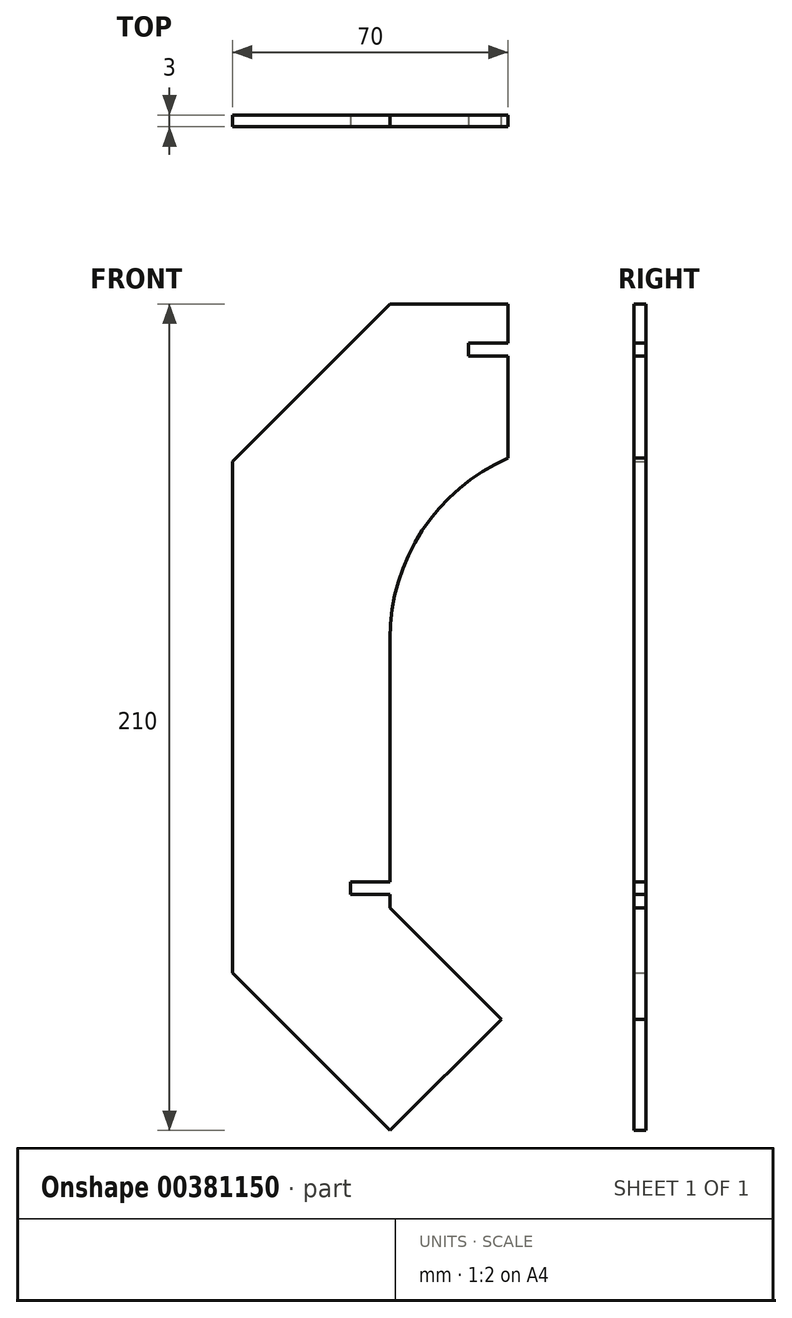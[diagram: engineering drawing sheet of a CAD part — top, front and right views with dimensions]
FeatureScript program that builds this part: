
annotation { "Feature Type Name" : "Feature", "Feature Type Description" : "" }
export const myFeature = defineFeature(function(context is Context, id is Id, definition is map)
    precondition{}
    {
        {
            var Q0;
            Q0=qCreatedBy(makeId("Front.planeOp"),FACE);
            var sketch = newSketch(context, id + "F0", { "sketchPlane" : qUnion([Q0])});
            skLineSegment(sketch, "E0", {"start": v(0, 0) * mm, "end": v(-50, 0) * mm});
            skLineSegment(sketch, "E1", {"start": v(-50, 0) * mm, "end": v(-90, -40) * mm});
            skLineSegment(sketch, "E2", {"start": v(-90, -40) * mm, "end": v(-90, -170) * mm});
            skLineSegment(sketch, "E3", {"start": v(-90, -170) * mm, "end": v(-50, -210) * mm});
            skLineSegment(sketch, "E4", {"start": v(-50, -210) * mm, "end": v(-21.72, -181.72) * mm});
            skLineSegment(sketch, "E5", {"start": v(-21.72, -181.72) * mm, "end": v(-50, -153.43) * mm});
            skArc(sketch, "E6", {"start": v(0, -35) * mm, "mid": v(-35.36, -49.64) * mm, "end": v(-50, -85) * mm});
            skLineSegment(sketch, "E7", {"start": v(-50, -85) * mm, "end": v(-50, -153.43) * mm});
            skLineSegment(sketch, "E8", {"start": v(0, 0) * mm, "end": v(0, -35) * mm});
            skSolve(sketch);
        }
        {
            var Q0;
            Q0=makeQuery(id+"F0.imprint","IMPRINT",FACE,{"disambiguationData":[TD([[makeQuery(id+"F0.imprint","IMPRINT",EDGE,{"derivedFrom":sQuery(id+"F0.wireOp",EDGE,"E0")}),1.0]])]});
            extrude(context, id + "F1", {"entities" : qUnion([Q0]), "endBound" : BoundingType.SYMMETRIC, "depth" : 3 * mm, "offsetDistance" : 25 * mm});
        }
        {
            var Q0;
            Q0=makeQuery(id+"F1.opExtrude","CAP_FACE",FACE,{"disambiguationData":[OSD([sQuery(id+"F0.wireOp",EDGE,"E0"),sQuery(id+"F0.wireOp",EDGE,"E1"),sQuery(id+"F0.wireOp",EDGE,"E2"),sQuery(id+"F0.wireOp",EDGE,"E3"),sQuery(id+"F0.wireOp",EDGE,"E4"),sQuery(id+"F0.wireOp",EDGE,"E5"),sQuery(id+"F0.wireOp",EDGE,"E6"),sQuery(id+"F0.wireOp",EDGE,"E7"),sQuery(id+"F0.wireOp",EDGE,"E8")])],"isStart":false});
            var sketch = newSketch(context, id + "F2", { "sketchPlane" : qUnion([Q0])});
            skLineSegment(sketch, "E9", {"start": v(-20, 0) * mm, "end": v(-20, -10) * mm});
            skLineSegment(sketch, "E10", {"start": v(-20, -10) * mm, "end": v(-30, -10) * mm});
            skLineSegment(sketch, "E11", {"start": v(-30, -10) * mm, "end": v(-30, -13.2) * mm});
            skLineSegment(sketch, "E12", {"start": v(-30, -13.2) * mm, "end": v(-20, -13.2) * mm});
            skLineSegment(sketch, "E13", {"start": v(-20, -13.2) * mm, "end": v(-20, -39.17) * mm});
            skArc(sketch, "E14.0", {"start": v(0, -35) * mm, "mid": v(-10.22, -36.05) * mm, "end": v(-20, -39.17) * mm});
            skPoint(sketch, "E15.orphan", {"position": v(-50, -85) * mm});
            skLineSegment(sketch, "E16", {"start": v(-20, 0) * mm, "end": v(0, 0) * mm});
            skLineSegment(sketch, "E17", {"start": v(0, 0) * mm, "end": v(0, -35) * mm});
            skLineSegment(sketch, "E18", {"start": v(0, 0) * mm, "end": v(0, 26.78) * mm, "construction": true});
            skLineSegment(sketch, "E19.bottom", {"start": v(-60, -146.8) * mm, "end": v(-50, -146.8) * mm});
            skLineSegment(sketch, "E19.top", {"start": v(-60, -150) * mm, "end": v(-50, -150) * mm});
            skLineSegment(sketch, "E19.left", {"start": v(-60, -146.8) * mm, "end": v(-60, -150) * mm});
            skLineSegment(sketch, "E19.right", {"start": v(-50, -146.8) * mm, "end": v(-50, -150) * mm});
            skSolve(sketch);
        }
        {
            var Q0;
            Q0 = qSketchRegion(id + "F2", true);
            extrude(context, id + "F3", {"entities" : qUnion([Q0]), "operationType" : NewBodyOperationType.REMOVE, "endBound" : BoundingType.THROUGH_ALL, "oppositeDirection" : true, "depth" : 25 * mm});
        }
    });
